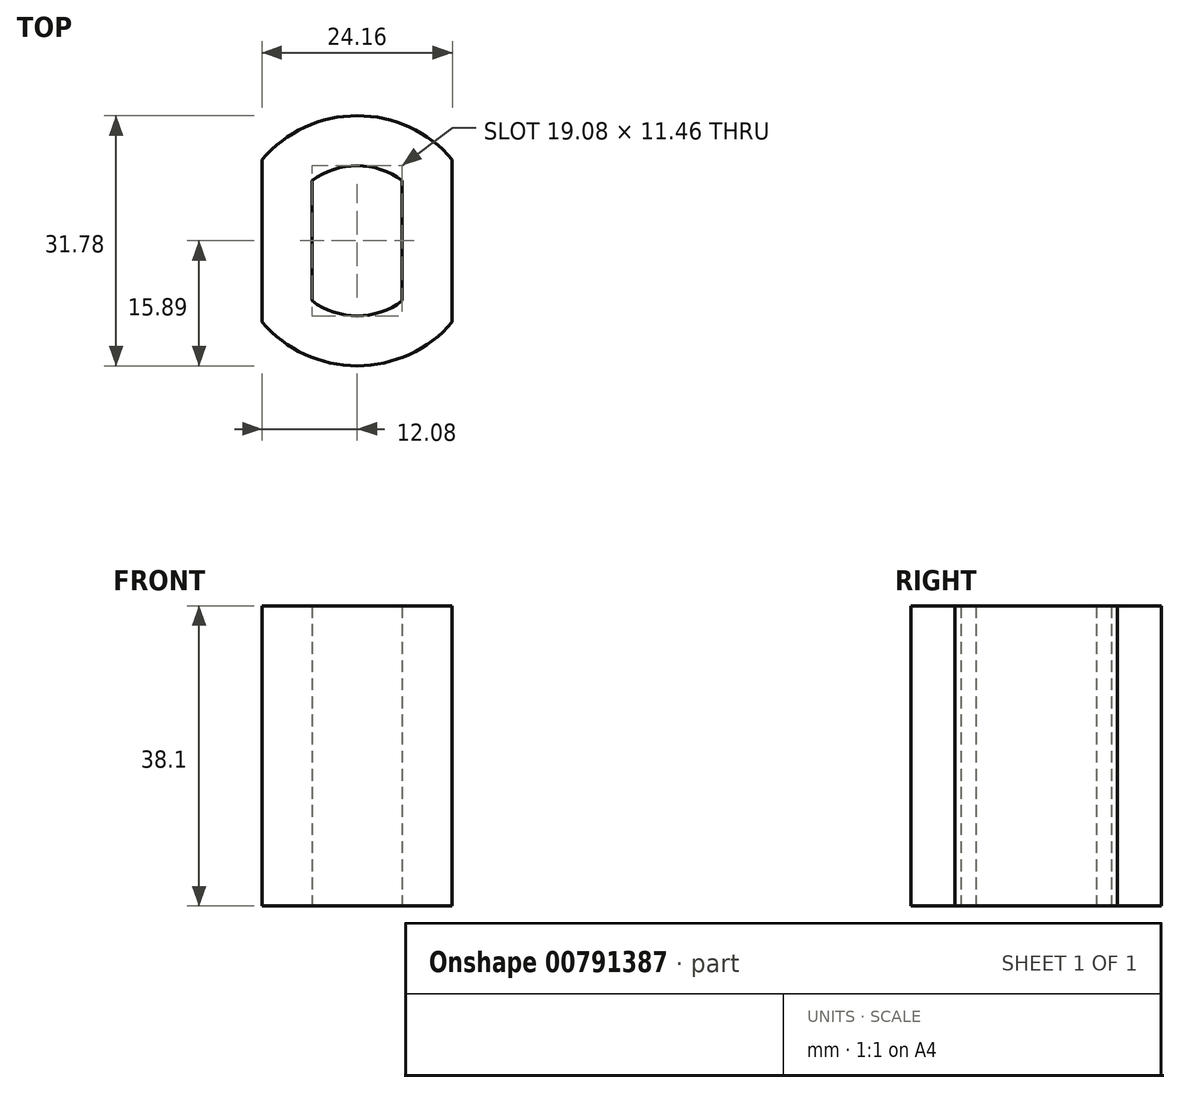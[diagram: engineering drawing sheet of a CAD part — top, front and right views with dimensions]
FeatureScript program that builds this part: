
annotation { "Feature Type Name" : "Feature", "Feature Type Description" : "" }
export const myFeature = defineFeature(function(context is Context, id is Id, definition is map)
    precondition{}
    {
        {
            var Q0;
            Q0=qCreatedBy(makeId("Top.planeOp"),FACE);
            var sketch = newSketch(context, id + "F0", { "sketchPlane" : qUnion([Q0])});
            skArc(sketch, "E0", {"start": v(-12.08, -10.32) * mm, "mid": v(0, -15.89) * mm, "end": v(12.08, -10.32) * mm});
            skCircle(sketch, "E1.0", {"center": v(0, 0) * mm, "radius": 18.43 * mm});
            skLineSegment(sketch, "E2", {"start": v(-12.08, 10.32) * mm, "end": v(-12.08, -10.32) * mm});
            skLineSegment(sketch, "E3", {"start": v(12.08, -10.32) * mm, "end": v(12.08, 10.32) * mm});
            skLineSegment(sketch, "E4", {"start": v(-32.32, 0) * mm, "end": v(26.82, 0) * mm, "construction": true});
            skPoint(sketch, "E4.endSnap0", {"position": v(12.08, 0) * mm});
            skPoint(sketch, "E5", {"position": v(-12.08, 0) * mm});
            skPoint(sketch, "E6", {"position": v(-15.89, 0) * mm});
            skArc(sketch, "E7.trimOffspring", {"start": v(12.08, 10.32) * mm, "mid": v(0, 15.89) * mm, "end": v(-12.08, 10.32) * mm});
            skArc(sketch, "E8.0", {"start": v(5.73, 7.63) * mm, "mid": v(0, 9.54) * mm, "end": v(-5.73, 7.63) * mm});
            skLineSegment(sketch, "E8.1", {"start": v(5.73, -7.63) * mm, "end": v(5.73, 7.63) * mm});
            skArc(sketch, "E8.2", {"start": v(-5.73, -7.63) * mm, "mid": v(0, -9.54) * mm, "end": v(5.73, -7.63) * mm});
            skLineSegment(sketch, "E8.3", {"start": v(-5.73, 7.63) * mm, "end": v(-5.73, -7.63) * mm});
            skSolve(sketch);
        }
        {
            var Q0;
            Q0=makeQuery(id+"F0.imprint","IMPRINT",FACE,{"disambiguationData":[TD([[makeQuery(id+"F0.imprint","IMPRINT",EDGE,{"derivedFrom":sQuery(id+"F0.wireOp",EDGE,"E0")}),1.0]])]});
            extrude(context, id + "F1", {"entities" : qUnion([Q0]), "depth" : 38.1 * mm, "offsetDistance" : 25.4 * mm});
        }
    });
